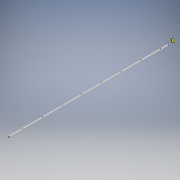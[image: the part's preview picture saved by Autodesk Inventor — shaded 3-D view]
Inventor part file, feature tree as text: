
AUTODESK INVENTOR PART (.ipt)
format: ipt  version: 2017 (Build 210142000, 142)  size: 132,608 bytes
history: native  units: mm
features: extrude x2, sketch x2
ambient origin geometry x8: Origin, YZ Plane, XZ Plane, XY Plane, X Axis, Y Axis, Z Axis, Center Point
bodies: Solid1 (feature_tree)
feature tree (4):
  extrude  "Extrusion1"  Depth=1.0mm
  extrude  "Extrusion2"  Depth=10.0mm TaperAngle=0.0deg
  sketch  "Sketch2"  dims[d0=22.0mm d1=1.0mm]
  sketch  "Sketch4"  dims[d2=2750.0mm d3=0.0mm d5=11.75mm d6=0.0mm d10=8.0mm d11=240.0mm d26=8.0mm d27=340.0mm d28=70.0mm d30=340.0mm d31=10.0mm d33=10.0mm]
